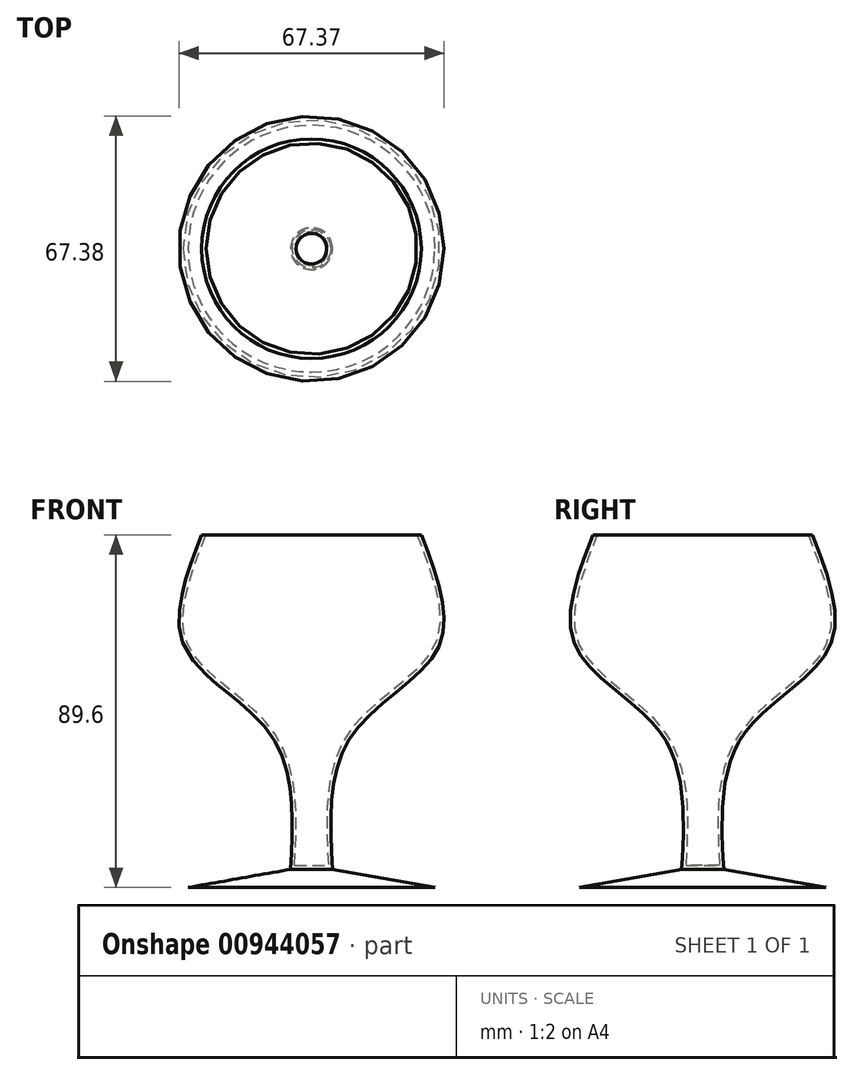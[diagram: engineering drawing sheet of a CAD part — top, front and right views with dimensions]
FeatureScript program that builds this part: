
annotation { "Feature Type Name" : "Feature", "Feature Type Description" : "" }
export const myFeature = defineFeature(function(context is Context, id is Id, definition is map)
    precondition{}
    {
        {
            var Q0;
            Q0=qCreatedBy(makeId("Top.planeOp"),FACE);
            var sketch = newSketch(context, id + "F0", { "sketchPlane" : qUnion([Q0])});
            skCircle(sketch, "E0", {"center": v(0, 0) * mm, "radius": 5.34 * mm});
            skSolve(sketch);
        }
        {
            var Q0;
            Q0=qCreatedBy(makeId("Top.planeOp"),FACE);
            cPlane(context, id + "F1", {"entities" : qUnion([Q0]), "cplaneType" : CPlaneType.OFFSET, "offset" : 85 * mm, "width" : 150 * mm, "height" : 150 * mm});
        }
        {
            var Q0;
            Q0=qCreatedBy(id+"F1.planeOp",FACE);
            var sketch = newSketch(context, id + "F2", { "sketchPlane" : qUnion([Q0])});
            skCircle(sketch, "E1", {"center": v(0, 0) * mm, "radius": 27.9 * mm});
            skSolve(sketch);
        }
        {
            var Q0;
            Q0=makeQuery(id+"F0.imprint","IMPRINT",FACE,{"disambiguationData":[TD([[makeQuery(id+"F0.imprint","IMPRINT",EDGE,{"derivedFrom":sQuery(id+"F0.wireOp",EDGE,"E0")}),1.0]])]});
            cPlane(context, id + "F3", {"entities" : qUnion([Q0]), "cplaneType" : CPlaneType.OFFSET, "offset" : 35 * mm, "width" : 150 * mm, "height" : 150 * mm});
        }
        {
            var Q0;
            Q0=makeQuery(id+"F0.imprint","IMPRINT",FACE,{"disambiguationData":[TD([[makeQuery(id+"F0.imprint","IMPRINT",EDGE,{"derivedFrom":sQuery(id+"F0.wireOp",EDGE,"E0")}),1.0]])]});
            cPlane(context, id + "F4", {"entities" : qUnion([Q0]), "cplaneType" : CPlaneType.OFFSET, "offset" : 57 * mm, "width" : 150 * mm, "height" : 150 * mm});
        }
        {
            var Q0;
            Q0=qCreatedBy(id+"F3.planeOp",FACE);
            var sketch = newSketch(context, id + "F5", { "sketchPlane" : qUnion([Q0])});
            skCircle(sketch, "E2", {"center": v(0, 0) * mm, "radius": 10.92 * mm});
            skSolve(sketch);
        }
        {
            var Q0;
            Q0=qCreatedBy(id+"F4.planeOp",FACE);
            var sketch = newSketch(context, id + "F6", { "sketchPlane" : qUnion([Q0])});
            skCircle(sketch, "E3", {"center": v(0, 0) * mm, "radius": 32.49 * mm});
            skSolve(sketch);
        }
        {
            var Q0;
            Q0=makeQuery(id+"F0.imprint","IMPRINT",FACE,{"disambiguationData":[TD([[makeQuery(id+"F0.imprint","IMPRINT",EDGE,{"derivedFrom":sQuery(id+"F0.wireOp",EDGE,"E0")}),1.0]])]});
            var Q1;
            Q1=makeQuery(id+"F5.imprint","IMPRINT",FACE,{"disambiguationData":[TD([[makeQuery(id+"F5.imprint","IMPRINT",EDGE,{"derivedFrom":sQuery(id+"F5.wireOp",EDGE,"E2")}),1.0]])]});
            var Q2;
            Q2=makeQuery(id+"F6.imprint","IMPRINT",FACE,{"disambiguationData":[TD([[makeQuery(id+"F6.imprint","IMPRINT",EDGE,{"derivedFrom":sQuery(id+"F6.wireOp",EDGE,"E3")}),1.0]])]});
            var Q3;
            Q3=makeQuery(id+"F2.imprint","IMPRINT",FACE,{"disambiguationData":[TD([[makeQuery(id+"F2.imprint","IMPRINT",EDGE,{"derivedFrom":sQuery(id+"F2.wireOp",EDGE,"E1")}),1.0]])]});
            loft(context, id + "F7", {"sheetProfilesArray" : [{ "sheetProfileEntities" : qUnion([Q0]) }, { "sheetProfileEntities" : qUnion([Q1]) }, { "sheetProfileEntities" : qUnion([Q2]) }, { "sheetProfileEntities" : qUnion([Q3]) }]});
        }
        {
            var Q0;
            Q0=makeQuery(id+"F7.opLoft","CAP_FACE",FACE,{"disambiguationData":[OSD([makeQuery(id+"F2.imprint","IMPRINT",FACE,{"disambiguationData":[TD([[makeQuery(id+"F2.imprint","IMPRINT",EDGE,{"derivedFrom":sQuery(id+"F2.wireOp",EDGE,"E1")}),1.0]])]})])],"isStart":true});
            shell(context, id + "F8", {"entities" : qUnion([Q0]), "thickness" : 1 * mm});
        }
        {
            var Q0;
            Q0=makeQuery(id+"F7.opLoft","CAP_FACE",FACE,{"disambiguationData":[OSD([makeQuery(id+"F0.imprint","IMPRINT",FACE,{"disambiguationData":[TD([[makeQuery(id+"F0.imprint","IMPRINT",EDGE,{"derivedFrom":sQuery(id+"F0.wireOp",EDGE,"E0")}),1.0]])]})])],"isStart":true});
            var sketch = newSketch(context, id + "F9", { "sketchPlane" : qUnion([Q0])});
            skCircle(sketch, "E4", {"center": v(0, 0) * mm, "radius": 5.26 * mm});
            skSolve(sketch);
        }
        {
            var Q0;
            Q0=makeQuery(id+"F9.imprint","IMPRINT",FACE,{"disambiguationData":[TD([[makeQuery(id+"F9.imprint","IMPRINT",EDGE,{"derivedFrom":sQuery(id+"F9.wireOp",EDGE,"E4")}),1.0]])]});
            extrude(context, id + "F10", {"entities" : qUnion([Q0]), "operationType" : NewBodyOperationType.ADD, "depth" : 4.6 * mm, "offsetDistance" : 25 * mm, "hasDraft" : true, "draftAngle" : 80 * degree});
        }
    });
